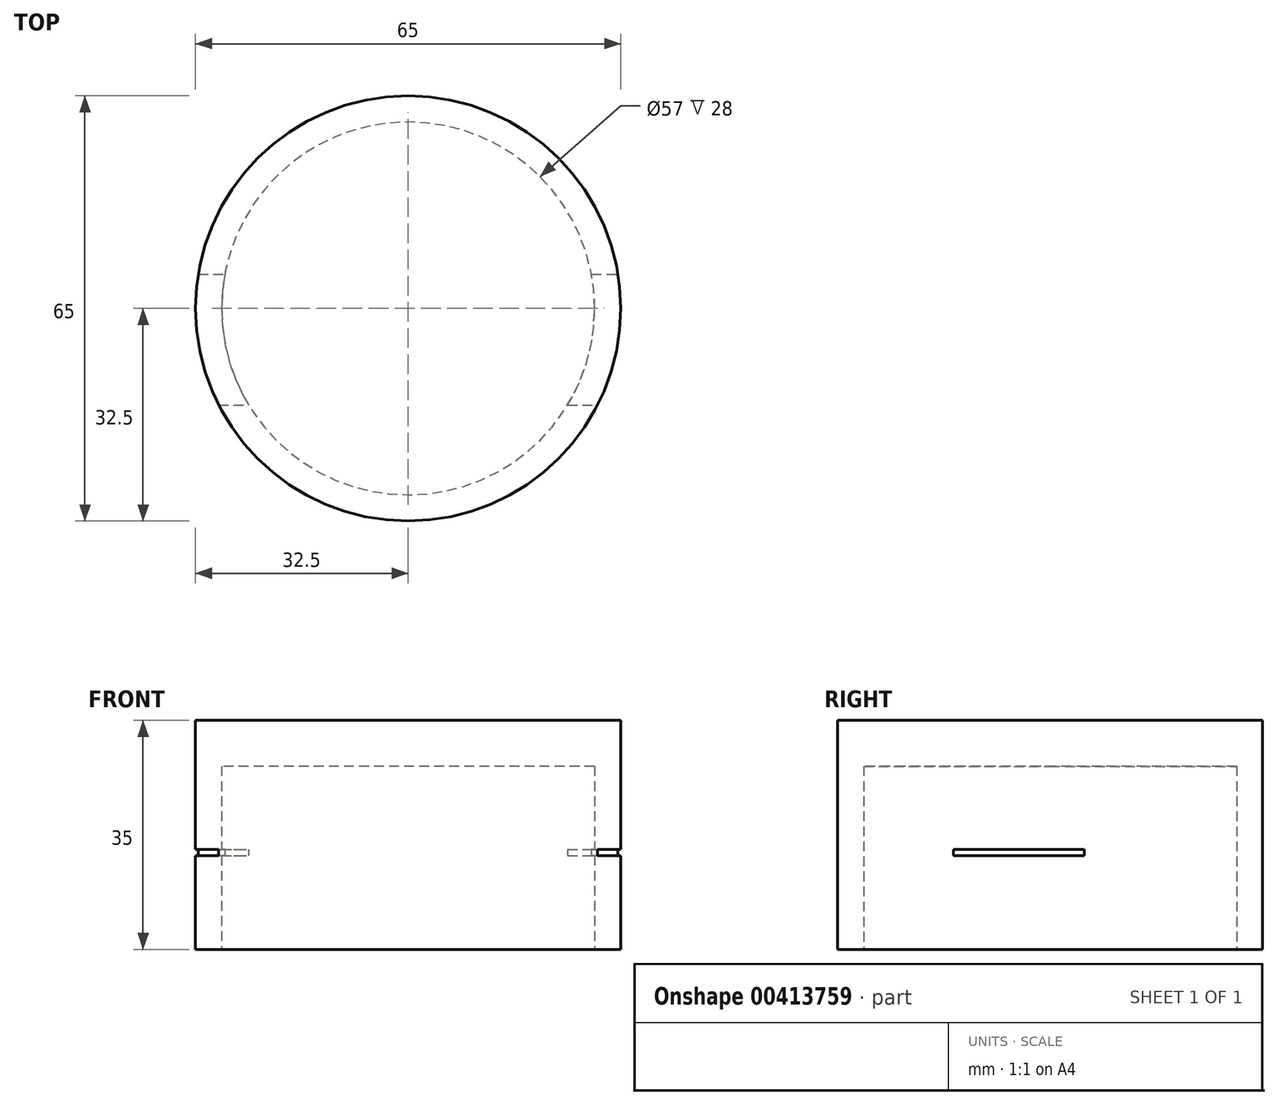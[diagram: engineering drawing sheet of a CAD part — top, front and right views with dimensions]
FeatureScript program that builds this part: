
annotation { "Feature Type Name" : "Feature", "Feature Type Description" : "" }
export const myFeature = defineFeature(function(context is Context, id is Id, definition is map)
    precondition{}
    {
        {
            var Q0;
            Q0=qCreatedBy(makeId("Top.planeOp"),FACE);
            var sketch = newSketch(context, id + "F0", { "sketchPlane" : qUnion([Q0])});
            skCircle(sketch, "E0", {"center": v(0, 0) * mm, "radius": 28.5 * mm});
            skSolve(sketch);
        }
        {
            var Q0;
            Q0=qCreatedBy(makeId("Top.planeOp"),FACE);
            var sketch = newSketch(context, id + "F1", { "sketchPlane" : qUnion([Q0])});
            skCircle(sketch, "E1", {"center": v(0, 0) * mm, "radius": 32.5 * mm});
            skSolve(sketch);
        }
        {
            var Q0;
            Q0 = qSketchRegion(id + "F1", true);
            extrude(context, id + "F2", {"entities" : qUnion([Q0]), "depth" : 35 * mm});
        }
        {
            var Q0;
            Q0 = qSketchRegion(id + "F0", true);
            extrude(context, id + "F3", {"entities" : qUnion([Q0]), "operationType" : NewBodyOperationType.REMOVE, "depth" : 28 * mm});
        }
        {
            var Q0;
            Q0=qCreatedBy(makeId("Right.planeOp"),FACE);
            var sketch = newSketch(context, id + "F4", { "sketchPlane" : qUnion([Q0])});
            skLineSegment(sketch, "E2.bottom", {"start": v(5.25, 14.3) * mm, "end": v(-14.75, 14.3) * mm});
            skLineSegment(sketch, "E2.top", {"start": v(5.25, 15.3) * mm, "end": v(-14.75, 15.3) * mm});
            skLineSegment(sketch, "E2.left", {"start": v(5.25, 14.3) * mm, "end": v(5.25, 15.3) * mm});
            skLineSegment(sketch, "E2.right", {"start": v(-14.75, 14.3) * mm, "end": v(-14.75, 15.3) * mm});
            skSolve(sketch);
        }
        {
            var Q0;
            Q0 = qSketchRegion(id + "F4", true);
            var Q1;
            Q1=makeQuery(id+"F2.opExtrude","SWEPT_FACE",FACE,{"disambiguationData":[OSD([sQuery(id+"F1.wireOp",EDGE,"E1")])]});
            extrude(context, id + "F5", {"entities" : qUnion([Q0]), "operationType" : NewBodyOperationType.REMOVE, "oppositeDirection" : true, "depth" : 40 * mm, "hasSecondDirection" : true, "secondDirectionBound" : SecondDirectionBoundingType.UP_TO_SURFACE, "secondDirectionOppositeDirection" : false, "secondDirectionBoundEntityFace" : qUnion([Q1]), "secondDirectionDepth" : 25 * mm});
        }
    });
